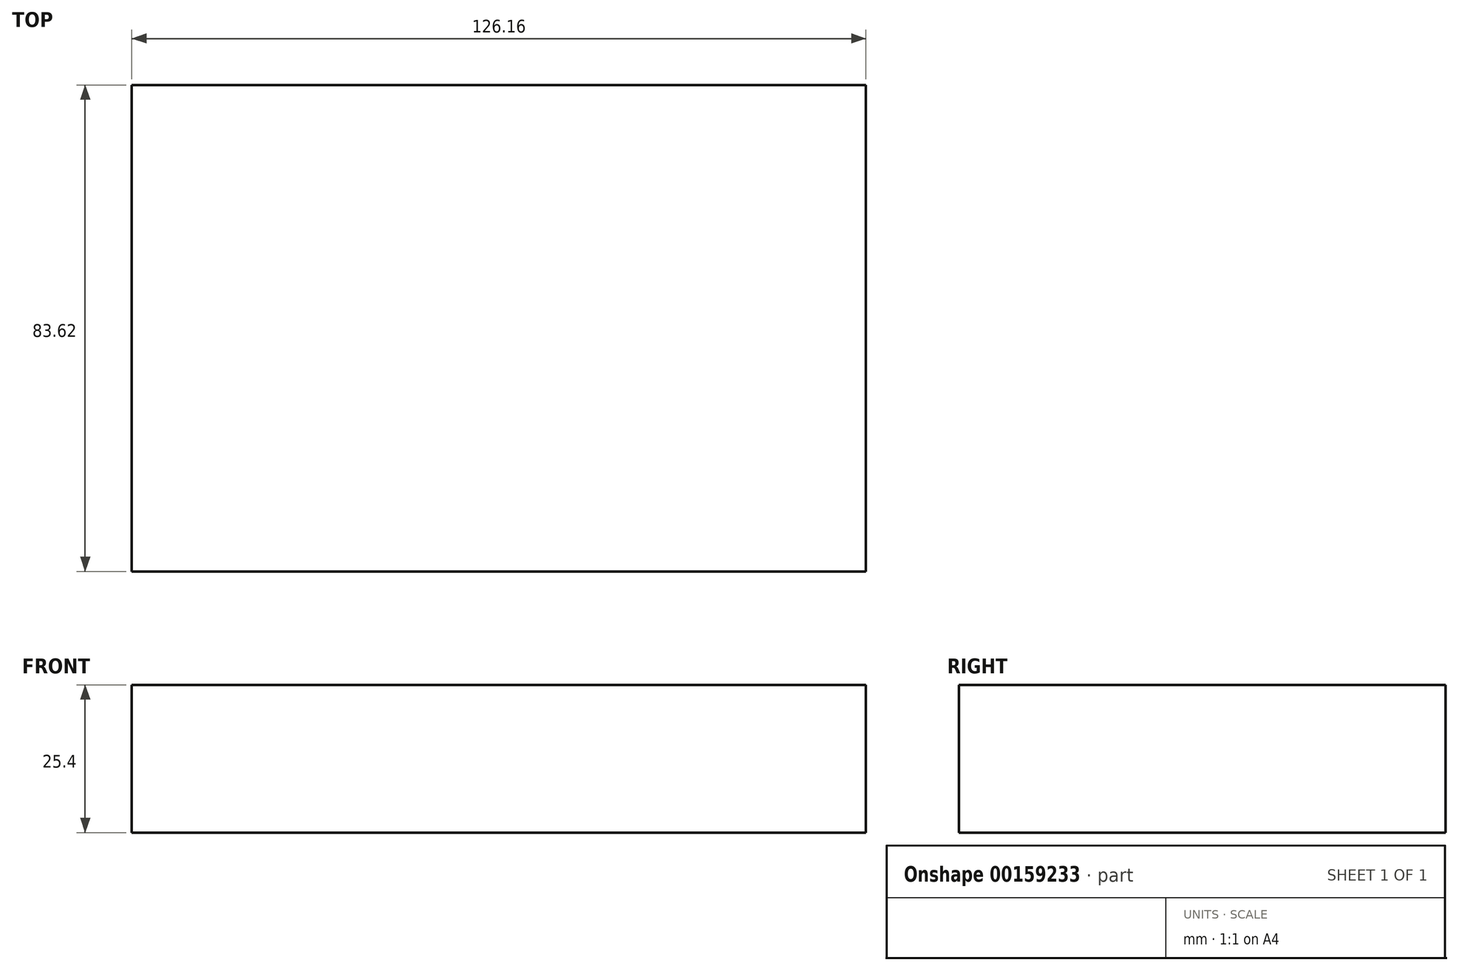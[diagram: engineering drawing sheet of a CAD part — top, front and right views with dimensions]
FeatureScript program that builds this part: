
annotation { "Feature Type Name" : "Feature", "Feature Type Description" : "" }
export const myFeature = defineFeature(function(context is Context, id is Id, definition is map)
    precondition{}
    {
        {
            var Q0;
            Q0=qCreatedBy(makeId("Top.planeOp"),FACE);
            var sketch = newSketch(context, id + "F0", { "sketchPlane" : qUnion([Q0])});
            skLineSegment(sketch, "E0.bottom", {"start": v(-61.92, -47.02) * mm, "end": v(64.24, -47.02) * mm});
            skLineSegment(sketch, "E0.top", {"start": v(-61.92, 36.6) * mm, "end": v(64.24, 36.6) * mm});
            skLineSegment(sketch, "E0.left", {"start": v(-61.92, -47.02) * mm, "end": v(-61.92, 36.6) * mm});
            skLineSegment(sketch, "E0.right", {"start": v(64.24, -47.02) * mm, "end": v(64.24, 36.6) * mm});
            skLineSegment(sketch, "E1", {"start": v(-61.92, -47.02) * mm, "end": v(-61.92, 32.53) * mm});
            skSolve(sketch);
        }
        {
            var Q0;
            Q0 = qSketchRegion(id + "F0", true);
            extrude(context, id + "F1", {"entities" : qUnion([Q0]), "depth" : 25.4 * mm});
        }
    });
